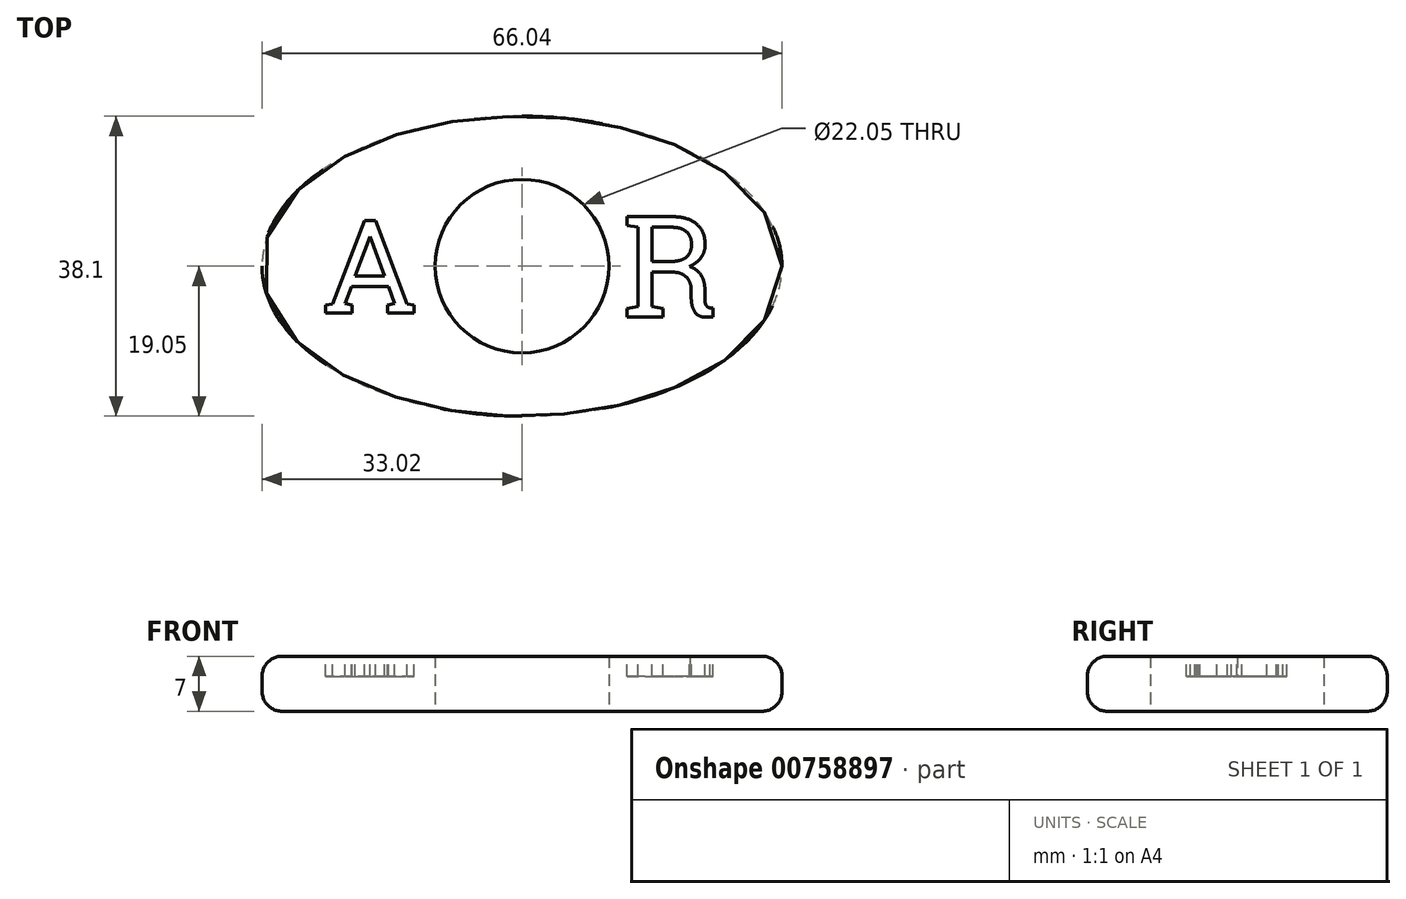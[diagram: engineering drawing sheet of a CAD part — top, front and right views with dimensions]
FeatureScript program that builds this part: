
annotation { "Feature Type Name" : "Feature", "Feature Type Description" : "" }
export const myFeature = defineFeature(function(context is Context, id is Id, definition is map)
    precondition{}
    {
        {
            var Q0;
            Q0=qCreatedBy(makeId("Top.planeOp"),FACE);
            var sketch = newSketch(context, id + "F0", { "sketchPlane" : qUnion([Q0])});
            skEllipse(sketch, "E0", {"center": v(0, 0) * mm, "majorRadius": 33.02 * mm, "minorRadius": 19.05 * mm, "majorAxis": v(1, 0)});
            skCircle(sketch, "E1", {"center": v(0, 0) * mm, "radius": 11.03 * mm});
            skLineSegment(sketch, "E2", {"start": v(-33.02, 0) * mm, "end": v(33.02, 0) * mm, "construction": true});
            skLineSegment(sketch, "E3", {"start": v(0, 19.05) * mm, "end": v(0, -19.05) * mm, "construction": true});
            skSolve(sketch);
        }
        {
            var Q0;
            Q0=makeQuery(id+"F0.imprint","IMPRINT",FACE,{"disambiguationData":[TD([[makeQuery(id+"F0.imprint","IMPRINT",EDGE,{"derivedFrom":sQuery(id+"F0.wireOp",EDGE,"E0")}),1.0]])]});
            extrude(context, id + "F1", {"entities" : qUnion([Q0]), "depth" : 7 * mm, "offsetDistance" : 25.4 * mm});
        }
        {
            var Q0;
            Q0=makeQuery(id+"F1.opExtrude","CAP_EDGE",EDGE,{"disambiguationData":[OSD([sQuery(id+"F0.wireOp",EDGE,"E0")])],"isStart":false});
            var Q1;
            Q1=makeQuery(id+"F1.opExtrude","CAP_EDGE",EDGE,{"disambiguationData":[OSD([sQuery(id+"F0.wireOp",EDGE,"E0")])],"isStart":true});
            fillet(context, id + "F2", {"entities" : qUnion([Q0, Q1]), "radius" : 2.54 * mm, "tangentPropagation" : true, "allowEdgeOverflow" : false});
        }
        {
            var Q0;
            Q0=makeQuery(id+"F1.opExtrude","CAP_FACE",FACE,{"disambiguationData":[OSD([sQuery(id+"F0.wireOp",EDGE,"E0"),sQuery(id+"F0.wireOp",EDGE,"E1")])],"isStart":false});
            var sketch = newSketch(context, id + "F3", { "sketchPlane" : qUnion([Q0])});
            skSolve(sketch);
        }
        {
            var Q0;
            {var subQ0=sQuery(id+"F0.wireOp",EDGE,"E1");Q0=makeQuery(id+"F3.imprint","IMPRINT",FACE,{"disambiguationData":[TD([[makeQuery(id+"F3.imprint","IMPRINT",EDGE,{"derivedFrom":makeQuery(id+"F1.opExtrude","CAP_EDGE",EDGE,{"disambiguationData":[OSD([subQ0])],"isStart":false})}),-1.0]])]});}
            var sketch = newSketch(context, id + "F4", { "sketchPlane" : qUnion([Q0])});
            skText(sketch, "E4", { "text": "A", "fontName": "RobotoSlab-Regular.ttf"});
            skText(sketch, "E5", { "text": "R", "fontName": "RobotoSlab-Regular.ttf"});
            skLineSegment(sketch, "E6", {"start": v(0, 0) * mm, "end": v(-25.4, 0) * mm, "construction": true});
            skLineSegment(sketch, "E7", {"start": v(0, 0) * mm, "end": v(25.4, 0) * mm, "construction": true});
            skLineSegment(sketch, "E8", {"start": v(-25.4, 0) * mm, "end": v(-12.7, 0) * mm, "construction": true});
            skLineSegment(sketch, "E9", {"start": v(12.7, 0) * mm, "end": v(25.4, 0) * mm});
            skPoint(sketch, "E10", {"position": v(19.05, 0) * mm});
            skLineSegment(sketch, "E11", {"start": v(12.7, 0) * mm, "end": v(25.4, 0) * mm, "construction": true});
            skPoint(sketch, "E12", {"position": v(-19.05, 0) * mm});
            const initialGuessF4  = {"E4": [-0.0254, -0.00594, 1, 0, 0.01189], "E5": [0.0127, -0.00648, 1, 0, 0.01295]};
            skSetInitialGuess(sketch, initialGuessF4);
            skSolve(sketch);
        }
        {
            var Q0;
            Q0=qSketchRegion(id+"F4",true);
            extrude(context, id + "F5", {"entities" : qUnion([Q0]), "operationType" : NewBodyOperationType.REMOVE, "oppositeDirection" : true, "depth" : 2.54 * mm, "offsetDistance" : 25.4 * mm});
        }
    });
